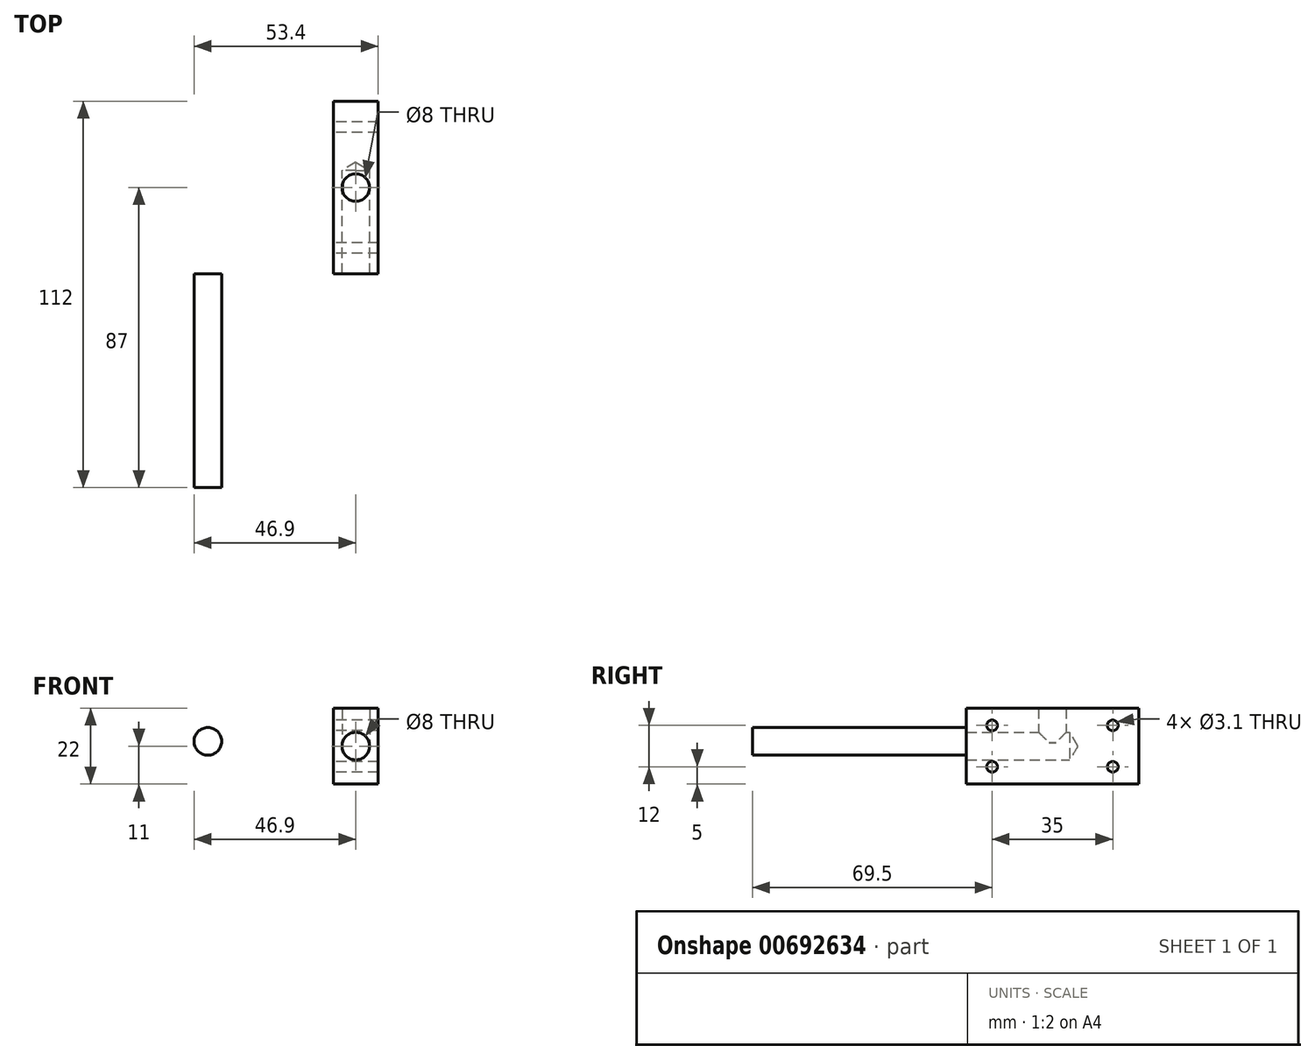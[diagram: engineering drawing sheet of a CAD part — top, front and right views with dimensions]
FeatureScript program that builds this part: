
annotation { "Feature Type Name" : "Feature", "Feature Type Description" : "" }
export const myFeature = defineFeature(function(context is Context, id is Id, definition is map)
    precondition{}
    {
        {
            var Q0;
            Q0=qCreatedBy(makeId("Right.planeOp"),FACE);
            var sketch = newSketch(context, id + "F0", { "sketchPlane" : qUnion([Q0])});
            skLineSegment(sketch, "E0.bottom", {"start": v(0, 0) * mm, "end": v(50, 0) * mm});
            skLineSegment(sketch, "E0.top", {"start": v(0, 22) * mm, "end": v(50, 22) * mm});
            skLineSegment(sketch, "E0.left", {"start": v(0, 0) * mm, "end": v(0, 22) * mm});
            skLineSegment(sketch, "E0.right", {"start": v(50, 0) * mm, "end": v(50, 22) * mm});
            skLineSegment(sketch, "E1", {"start": v(7.5, 17) * mm, "end": v(42.5, 17) * mm, "construction": true});
            skCircle(sketch, "E2", {"center": v(7.5, 17) * mm, "radius": 1.55 * mm});
            skLineSegment(sketch, "E3", {"start": v(7.5, 17) * mm, "end": v(7.5, 5) * mm, "construction": true});
            skCircle(sketch, "E4", {"center": v(7.5, 5) * mm, "radius": 1.55 * mm});
            skLineSegment(sketch, "E5", {"start": v(42.5, 17) * mm, "end": v(42.5, 5) * mm, "construction": true});
            skCircle(sketch, "E6", {"center": v(42.5, 17) * mm, "radius": 1.55 * mm});
            skCircle(sketch, "E7", {"center": v(42.5, 5) * mm, "radius": 1.55 * mm});
            skSolve(sketch);
        }
        {
            var Q0;
            Q0=makeQuery(id+"F0.imprint","IMPRINT",FACE,{"disambiguationData":[TD([[makeQuery(id+"F0.imprint","IMPRINT",EDGE,{"derivedFrom":sQuery(id+"F0.wireOp",EDGE,"E0.bottom")}),1.0]])]});
            extrude(context, id + "F1", {"entities" : qUnion([Q0]), "depth" : 13 * mm, "offsetDistance" : 25 * mm});
        }
        {
            var Q0;
            Q0=makeQuery(id+"F1.opExtrude","SWEPT_FACE",FACE,{"disambiguationData":[OSD([sQuery(id+"F0.wireOp",EDGE,"E0.left")])]});
            var sketch = newSketch(context, id + "F2", { "sketchPlane" : qUnion([Q0])});
            skLineSegment(sketch, "E8", {"start": v(6.5, 22) * mm, "end": v(6.5, 0) * mm, "construction": true});
            skLineSegment(sketch, "E9", {"start": v(0, 11) * mm, "end": v(13, 11) * mm, "construction": true});
            skCircle(sketch, "E10", {"center": v(6.5, 11) * mm, "radius": 4 * mm});
            skSolve(sketch);
        }
        {
            var Q0;
            Q0=sQuery(id+"F2.wireOp",VERTEX,"E10.center");
            var Q1;
            Q1=makeQuery(id+"F1.opExtrude","SWEPT_BODY",BODY,{"disambiguationData":[OSD([sQuery(id+"F0.wireOp",EDGE,"E0.bottom"),sQuery(id+"F0.wireOp",EDGE,"E0.top"),sQuery(id+"F0.wireOp",EDGE,"E0.left"),sQuery(id+"F0.wireOp",EDGE,"E0.right"),sQuery(id+"F0.wireOp",EDGE,"E2"),sQuery(id+"F0.wireOp",EDGE,"dc547574-addc-4ca1-8533-5b690f575ed5.1.0.0"),sQuery(id+"F0.wireOp",EDGE,"IOKy1O9x-cp9w-2pif-nloN-PmFf7KNNbEXF"),sQuery(id+"F0.wireOp",EDGE,"3e3adc3b-3ffd-4f0e-b872-09c4254f0dde.1.0.0")])]});
            hole(context, id + "F3", {"style" : HoleStyle.SIMPLE, "endStyle" : HoleEndStyle.BLIND, "holeDiameter" : 8 * mm, "majorDiameter" : 5 * mm, "holeDepth" : 30 * mm, "isTappedThrough" : true, "tappedDepth" : 12 * mm, "tapClearance" : 3, "locations" : qUnion([Q0]), "scope" : qUnion([Q1])});
        }
        {
            var Q0;
            Q0=qCreatedBy(makeId("Front.planeOp"),FACE);
            var sketch = newSketch(context, id + "F4", { "sketchPlane" : qUnion([Q0])});
            skCircle(sketch, "E11", {"center": v(-36.4, 12.38) * mm, "radius": 4 * mm});
            skSolve(sketch);
        }
        {
            var Q0;
            Q0 = qSketchRegion(id + "F4", true);
            extrude(context, id + "F5", {"entities" : qUnion([Q0]), "depth" : 62 * mm, "offsetDistance" : 25 * mm});
        }
        {
            var Q0;
            Q0=makeQuery(id+"F1.opExtrude","SWEPT_FACE",FACE,{"disambiguationData":[OSD([sQuery(id+"F0.wireOp",EDGE,"E0.top")])]});
            var sketch = newSketch(context, id + "F6", { "sketchPlane" : qUnion([Q0])});
            skLineSegment(sketch, "E12", {"start": v(6.5, 50) * mm, "end": v(6.5, 0) * mm, "construction": true});
            skLineSegment(sketch, "E13", {"start": v(13, 25) * mm, "end": v(0, 25) * mm, "construction": true});
            skCircle(sketch, "E14", {"center": v(6.5, 25) * mm, "radius": 1.54 * mm});
            skSolve(sketch);
        }
        {
            var Q0;
            Q0=sQuery(id+"F6.wireOp",VERTEX,"E14.center");
            var Q1;
            Q1=makeQuery(id+"F1.opExtrude","SWEPT_BODY",BODY,{"disambiguationData":[OSD([sQuery(id+"F0.wireOp",EDGE,"E0.bottom"),sQuery(id+"F0.wireOp",EDGE,"E0.top"),sQuery(id+"F0.wireOp",EDGE,"E0.left"),sQuery(id+"F0.wireOp",EDGE,"E0.right"),sQuery(id+"F0.wireOp",EDGE,"E2"),sQuery(id+"F0.wireOp",EDGE,"E4"),sQuery(id+"F0.wireOp",EDGE,"E6"),sQuery(id+"F0.wireOp",EDGE,"E7")])]});
            hole(context, id + "F7", {"style" : HoleStyle.SIMPLE, "endStyle" : HoleEndStyle.BLIND, "holeDiameter" : 8 * mm, "majorDiameter" : 5 * mm, "holeDepth" : 10 * mm, "isTappedThrough" : true, "tappedDepth" : 12 * mm, "tapClearance" : 3, "locations" : qUnion([Q0]), "scope" : qUnion([Q1])});
        }
    });
